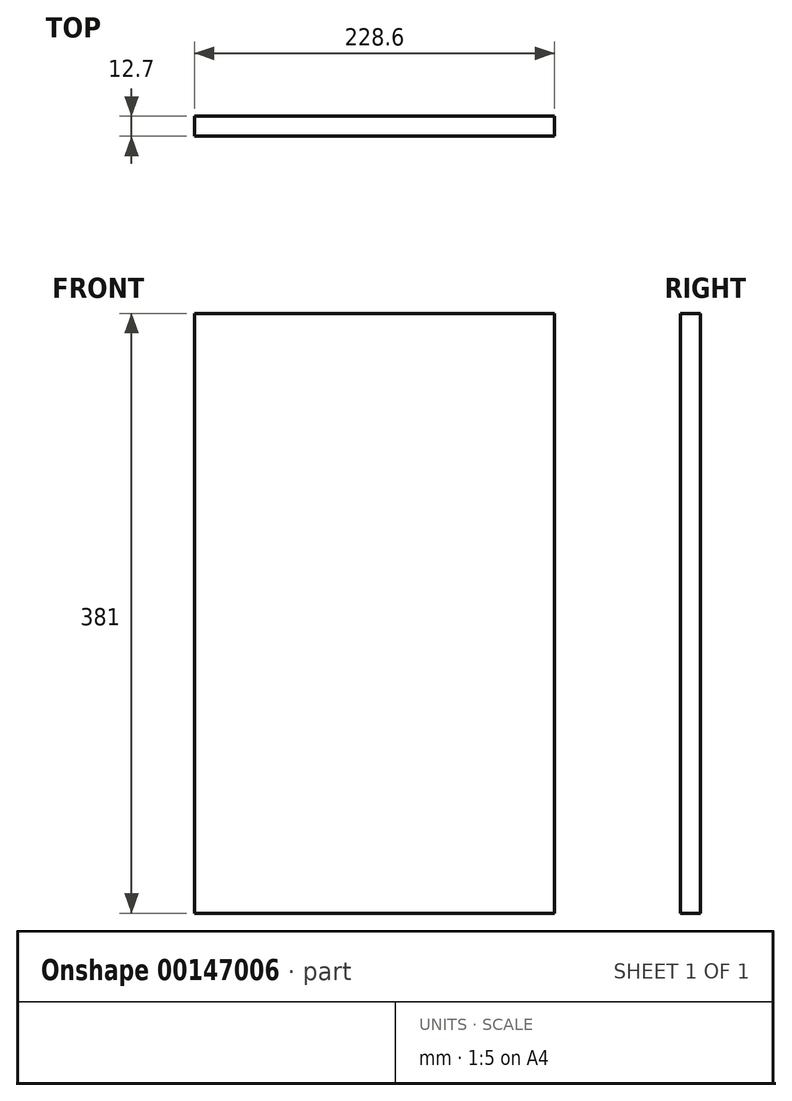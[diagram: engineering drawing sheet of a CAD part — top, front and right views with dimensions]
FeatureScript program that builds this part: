
annotation { "Feature Type Name" : "Feature", "Feature Type Description" : "" }
export const myFeature = defineFeature(function(context is Context, id is Id, definition is map)
    precondition{}
    {
        {
            var Q0;
            Q0=qCreatedBy(makeId("Front.planeOp"),FACE);
            var sketch = newSketch(context, id + "F0", { "sketchPlane" : qUnion([Q0])});
            skLineSegment(sketch, "E0.bottom", {"start": v(-177.18, 341.01) * mm, "end": v(51.42, 341.01) * mm});
            skLineSegment(sketch, "E0.top", {"start": v(-177.18, -39.99) * mm, "end": v(51.42, -39.99) * mm});
            skLineSegment(sketch, "E0.left", {"start": v(-177.18, 341.01) * mm, "end": v(-177.18, -39.99) * mm});
            skLineSegment(sketch, "E0.right", {"start": v(51.42, 341.01) * mm, "end": v(51.42, -39.99) * mm});
            skSolve(sketch);
        }
        {
            var Q0;
            Q0=makeQuery(id+"F0.imprint","IMPRINT",FACE,{"disambiguationData":[TD([[makeQuery(id+"F0.imprint","IMPRINT",EDGE,{"derivedFrom":sQuery(id+"F0.wireOp",EDGE,"E0.bottom")}),-1.0]])]});
            extrude(context, id + "F1", {"entities" : qUnion([Q0]), "depth" : 12.7 * mm});
        }
    });
